# Revit family: Construction_Other_Sjobergs_Wood_Lathe_Machine
name_source: partatom
category: Specialty Equipment
revit_build: Autodesk Revit 2017 (Build: 20190508_0315(x64)
units: mm (PartAtom-declared; Revit-internal decimal feet)

## family parameters
Always vertical = Yes
Cut with Voids When Loaded = No
OmniClass Number = 23.45.30.14.11
OmniClass Title = Commercial Dishwashers
Part Type = Normal
Room Calculation Point = No
Round Connector Dimension = Use Diameter
Shared = No
Work Plane-Based = No

## types (1)
- 37010 EJCA Wood Lathe TSL 30
    AssetType = Movable
    BIMObjectName = Construction_Other_Sjobergs_Wood_Lathe_Machine
    Brand = EJCA
    Category = Machines
    Color = Green
    Constituents = Protective Cover CHO 40 - Equipped with sight glass, built-in work lighting, connection socket for chip extraction and a roller in the front edge of the hood. Adjustament table (length 850-1250mm).
    ConvergoRefNr = 0184-2005-0025-SE
    Cost = 0 $
    DurationUnit = Year
    ElectricalDeviceNominalPower = 1500 W
    Features = The lathe spindle is drilled and mounted in conical precision roller bearings. The spindle speed is regulated steplessly with a knob on the control panel. CE-standard.
    Finish = Cast iron
    HasProtectiveEarth = Yes
    IP_Code = IP 66
    IfcExportAs = IfcFurnishingElementType
    IfcExportType = TABLE
    MachineryMainMaterial = Green metal
    MachineryQuaternaryMaterial = Clearance
    MachinerySecondaryMaterial = Black Metal
    MachineryTertiaryMaterial = Stainless Steel
    Manufacturer = Sjöbergs
    ManufacturerName = Sjöbergs
    ManufacturerURL = https://www.sjobergs.se
    Material = Metal, plastic
    Model = 37010 EJCA Wood Lathe TSL 30
    ModelReference = 37010
    NBSDescription = School art, design and technology tables and workbenches;
    NBSReference = 45-35-20/320
    Name = Sjobergs_Wood_Lathe_Machine
    NominalCurrent = 0 A
    NominalDepth = 480 mm
    NominalFrequencyRange = 0 Hz
    NominalHeight = 1320 mm  [stored 4.33071 ft]
    NominalVoltage = 230 V
    NominalWidth = 1630 mm
    NumberOfPoles = 0
    PhaseAngle = 0.00°
    ProductDatasheet = https://www.sjobergs.se
    ProductInformation = Wood lathe with stepless electronic speed control. A modern machine where technology and know-how have been combined into the market's most distinguished machine in its class.
    Shape = Sculptured
    Size = 1630x480x1320 mm
    SpindleSpeed = 80 - 2300 rpm
    SpindleThread = UNC1½ ”x6 mm
    URL = https://www.sjobergs.se
    Uniclass2 = Pr_40_50_21
    Uniclass2015Description = Desks, Tables And Worktops
    Uniclass2015Reference = Pr_40_50_21_76
    UsageCurrent = 0 A
    Version = 1
    VersionDate = 01/07/2020
    WarrantyDurationUnit = Year
    Weight = 350.0 kg
    WoodLatheSizes = Stud height 300 mm. Distance between drive and roller stud 270 mm. The total length of the lathe is about 950 mm. The total width of the lathe is about 400 mm. Height about 1200 m on all models.

note: [stored X ft] marks values corroborated as IEEE doubles in the binary element streams (Revit-internal decimal feet)

## geometry (parser evidence)
native form markers: Sweep x5
no freeform markers — native parametric forms only
